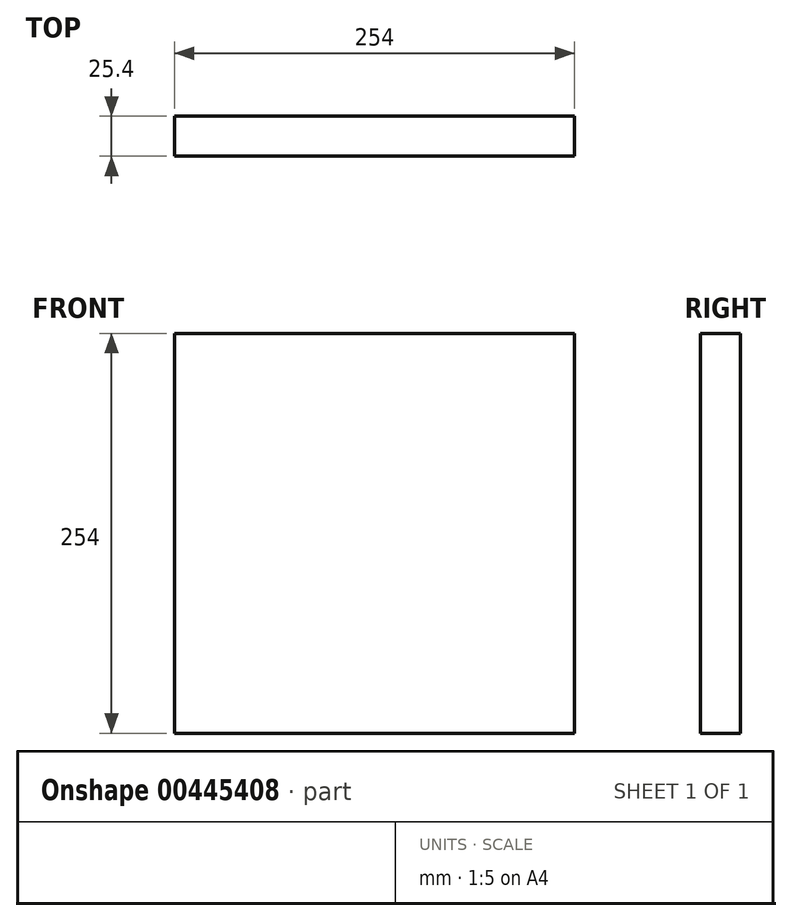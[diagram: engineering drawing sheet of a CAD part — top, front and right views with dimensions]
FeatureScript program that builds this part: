
annotation { "Feature Type Name" : "Feature", "Feature Type Description" : "" }
export const myFeature = defineFeature(function(context is Context, id is Id, definition is map)
    precondition{}
    {
        {
            var Q0;
            Q0=qCreatedBy(makeId("Front.planeOp"),FACE);
            var sketch = newSketch(context, id + "F0", { "sketchPlane" : qUnion([Q0])});
            skLineSegment(sketch, "E0.bottom", {"start": v(-127, 127) * mm, "end": v(127, 127) * mm});
            skLineSegment(sketch, "E0.top", {"start": v(-127, -127) * mm, "end": v(127, -127) * mm});
            skLineSegment(sketch, "E0.left", {"start": v(-127, 127) * mm, "end": v(-127, -127) * mm});
            skLineSegment(sketch, "E0.right", {"start": v(127, 127) * mm, "end": v(127, -127) * mm});
            skLineSegment(sketch, "E1", {"start": v(-127, 127) * mm, "end": v(127, -127) * mm, "construction": true});
            skSolve(sketch);
        }
        {
            var Q0;
            Q0=makeQuery(id+"F0.imprint","IMPRINT",FACE,{"disambiguationData":[TD([[makeQuery(id+"F0.imprint","IMPRINT",EDGE,{"derivedFrom":sQuery(id+"F0.wireOp",EDGE,"E0.bottom")}),-1.0]])]});
            extrude(context, id + "F1", {"entities" : qUnion([Q0]), "endBound" : BoundingType.SYMMETRIC, "depth" : 25.4 * mm});
        }
    });
